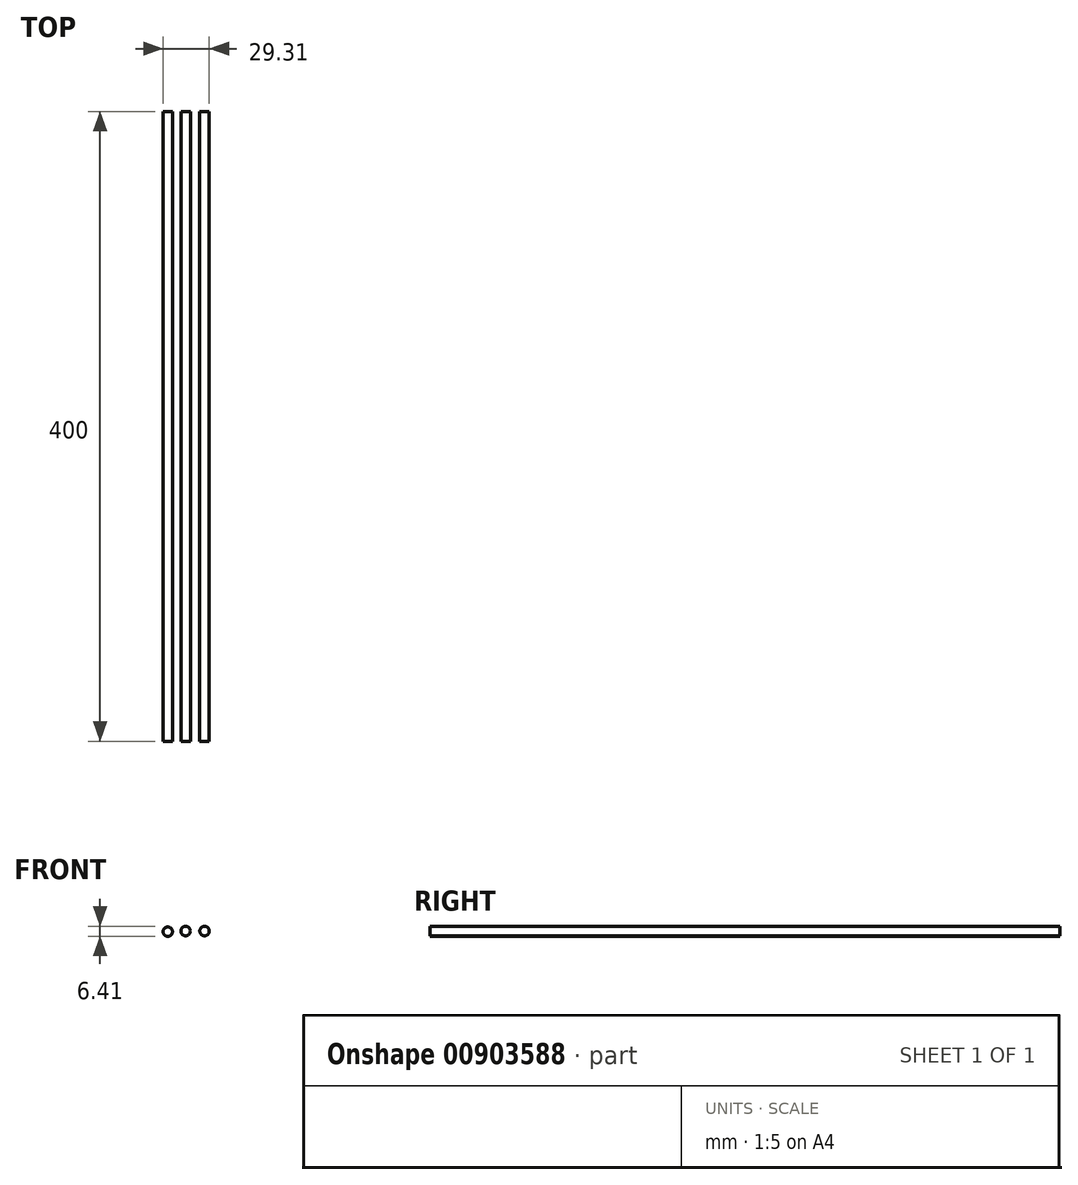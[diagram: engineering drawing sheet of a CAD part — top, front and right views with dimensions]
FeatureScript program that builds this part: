
annotation { "Feature Type Name" : "Feature", "Feature Type Description" : "" }
export const myFeature = defineFeature(function(context is Context, id is Id, definition is map)
    precondition{}
    {
        {
            var Q0;
            Q0=qCreatedBy(makeId("Front.planeOp"),FACE);
            var sketch = newSketch(context, id + "F0", { "sketchPlane" : qUnion([Q0])});
            skCircle(sketch, "E0", {"center": v(0, 0) * mm, "radius": 3 * mm});
            skSolve(sketch);
        }
        {
            var Q0;
            Q0=makeQuery(id+"F0.imprint","IMPRINT",FACE,{"disambiguationData":[TD([[makeQuery(id+"F0.imprint","IMPRINT",EDGE,{"derivedFrom":sQuery(id+"F0.wireOp",EDGE,"E0")}),1.0]])]});
            extrude(context, id + "F1", {"entities" : qUnion([Q0]), "endBound" : BoundingType.SYMMETRIC, "depth" : 400 * mm});
        }
        {
            var Q0;
            Q0=qCreatedBy(makeId("Front.planeOp"),FACE);
            var sketch = newSketch(context, id + "F2", { "sketchPlane" : qUnion([Q0])});
            skCircle(sketch, "E1", {"center": v(-12, 0) * mm, "radius": 3 * mm});
            skSolve(sketch);
        }
        {
            var Q0;
            Q0=qSketchRegion(id+"F2",true);
            extrude(context, id + "F3", {"entities" : qUnion([Q0]), "endBound" : BoundingType.SYMMETRIC, "depth" : 400 * mm});
        }
        {
            var Q0;
            Q0=qCreatedBy(makeId("Front.planeOp"),FACE);
            var sketch = newSketch(context, id + "F4", { "sketchPlane" : qUnion([Q0])});
            skCircle(sketch, "E2", {"center": v(-23.31, -0.4) * mm, "radius": 3 * mm});
            skSolve(sketch);
        }
        {
            var Q0;
            Q0=makeQuery(id+"F4.imprint","IMPRINT",FACE,{"disambiguationData":[TD([[makeQuery(id+"F4.imprint","IMPRINT",EDGE,{"derivedFrom":sQuery(id+"F4.wireOp",EDGE,"E2")}),1.0]])]});
            extrude(context, id + "F5", {"entities" : qUnion([Q0]), "endBound" : BoundingType.SYMMETRIC, "depth" : 400 * mm});
        }
    });
